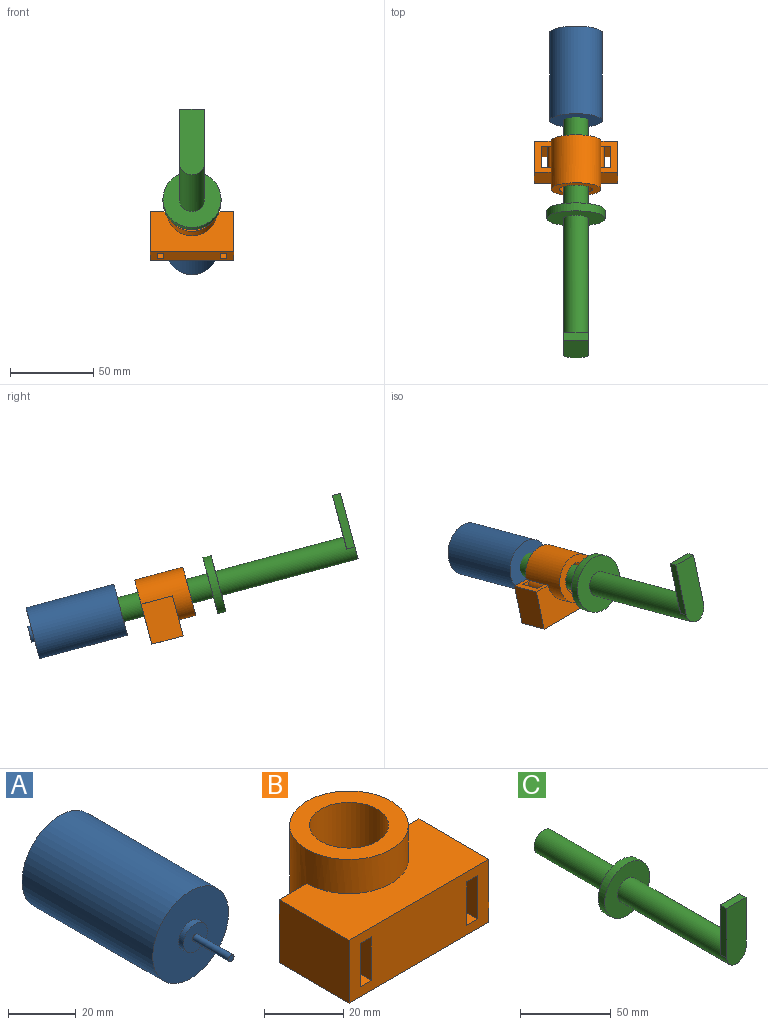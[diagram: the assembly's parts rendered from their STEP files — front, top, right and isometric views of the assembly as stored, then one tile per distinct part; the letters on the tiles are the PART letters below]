
ASSEMBLY  parts=3 mates=2
PART A: 9 faces, bbox 31.7x73.7x31.7 mm
  f0: cylinder r=5mm len=10mm, axis (0,1,0), area 62.8mm2, adj f1,f4
  f1: plane 10x10mm, normal (0,1,0), area 78.5mm2, adj f0
  f2: cylinder r=15.85mm len=54.7mm, axis (0,1,0), area 5447.5mm2, adj f3,f4
  f3: plane 31.7x31.7mm, normal (0,-1,0), area 710.7mm2, adj f2,f5
  f4: plane 31.7x31.7mm, normal (0,1,0), area 710.7mm2, adj f0,f2
  f5: cylinder r=5mm len=10mm, axis (0,1,0), area 62.8mm2, adj f3,f6
  f6: plane 10x10mm, normal (0,-1,0), area 74.4mm2, adj f5,f7
  f7: cylinder r=1.15mm len=15mm, axis (0,1,0), area 108.4mm2, adj f6,f8
  f8: plane 2.3x2.3mm, normal (0,-1,0), area 4.2mm2, adj f7
PART B: 20 faces, bbox 50x40x30 mm
  f0: plane 19.45x10mm, normal (0,1,0), area 113.8mm2, adj f2,f4,f7,f8,f10,f12,f13
  f1: plane 50x19.45mm, normal (0,-1,0), area 865.1mm2, adj f4,f6,f7,f8,f10,f11,f12,f13
  f2: cylinder r=15mm len=30mm, axis (0,0,-1), area 1910.7mm2, adj f0,f3,f4,f5,f7,f18,f19
  f3: plane 30x30mm, normal (0,0,1), area 392.7mm2, adj f2,f9
  f4: plane 50x40mm, normal (0,0,-1), area 1289.3mm2, adj f0,f1,f2,f5,f6,f8,f9
  f5: plane 19.45x10mm, normal (0,1,0), area 113.8mm2, adj f2,f4,f6,f7,f14,f15,f16
  f6: plane 25x19.45mm, normal (1,0,0), area 486.4mm2, adj f1,f4,f5,f7
  f7: plane 50x25mm, normal (0,0,1), area 896.6mm2, adj f0,f1,f2,f5,f6,f8
  f8: plane 25x19.45mm, normal (-1,0,0), area 486.4mm2, adj f0,f1,f4,f7
  f9: cylinder r=10mm len=30mm, axis (0,0,1), area 1885mm2, adj f3,f4
  f10: plane 25x6mm, normal (0,0,-1), area 102.4mm2, adj f0,f1,f11,f13,f18
  f11: plane 21x13.45mm, normal (-1,0,0), area 282.5mm2, adj f1,f10,f12,f18
  f12: plane 25x6mm, normal (0,0,1), area 102.4mm2, adj f0,f1,f11,f13,f18
  f13: plane 25x13.45mm, normal (1,0,0), area 336.4mm2, adj f0,f1,f10,f12
  f14: plane 25x6mm, normal (0,0,-1), area 102.4mm2, adj f1,f5,f15,f17,f19
  f15: plane 25x13.45mm, normal (-1,0,0), area 336.4mm2, adj f1,f5,f14,f16
  f16: plane 25x6mm, normal (0,0,1), area 102.4mm2, adj f1,f5,f15,f17,f19
  f17: plane 21x13.45mm, normal (1,0,0), area 282.5mm2, adj f1,f14,f16,f19
  f18: cylinder r=5mm len=13.45mm, axis (0,0,-1), area 62.4mm2, adj f2,f10,f11,f12
  f19: cylinder r=5mm len=13.45mm, axis (0,0,-1), area 62.4mm2, adj f2,f14,f16,f17
PART C: 13 faces, bbox 35x150x50.9 mm
  f0: cylinder r=7.5mm len=60mm, axis (0,1,0), area 2827.4mm2, adj f1,f6
  f1: plane 15x15mm, normal (0,1,0), area 172.2mm2, adj f0,f2
  f2: cylinder r=1.2mm len=15mm, axis (0,1,0), area 113.1mm2, adj f1,f3
  f3: plane 2.4x2.4mm, normal (0,1,0), area 4.5mm2, adj f2
  f4: cylinder r=17.5mm len=35mm, axis (0,1,0), area 549.8mm2, adj f5,f6
  f5: plane 35x35mm, normal (0,-1,0), area 785.4mm2, adj f4,f12
  f6: plane 35x35mm, normal (0,1,0), area 785.4mm2, adj f0,f4
  f7: plane 15x5mm, normal (0,0,1), area 75mm2, adj f8,f9,f10,f11
  f8: plane 40.89x15mm, normal (0,-1,0), area 589.2mm2, adj f7,f9,f11,f12
  f9: plane 33.39x5mm, normal (1,0,0), area 166.9mm2, adj f7,f8,f10,f12
  f10: plane 33.39x15mm, normal (0,1,0), area 412.5mm2, adj f7,f9,f11,f12
  f11: plane 33.39x5mm, normal (-1,0,0), area 166.9mm2, adj f7,f8,f10,f12
  f12: cylinder r=7.5mm len=85mm, axis (0,1,0), area 3887.7mm2, adj f5,f8,f9,f10,f11
PLACE A rot(axis=(-1,0,0),15deg) t=(-8.5,83.78,-25.56)mm
PLACE B rot(axis=(1,0,0),75deg) t=(-8.5,16.56,-7.55)mm
PLACE C rot(axis=(-1,0,0),15deg) t=(-8.5,32.79,-11.9)mm
MATE cylindrical C.f2 <-> A.f7  axis (0,0.97,-0.26) through (-8.5,18.3,-8.02)mm
MATE cylindrical B.f9 <-> C.f2  axis (0,-0.97,0.26) through (-8.5,16.56,-7.55)mm
